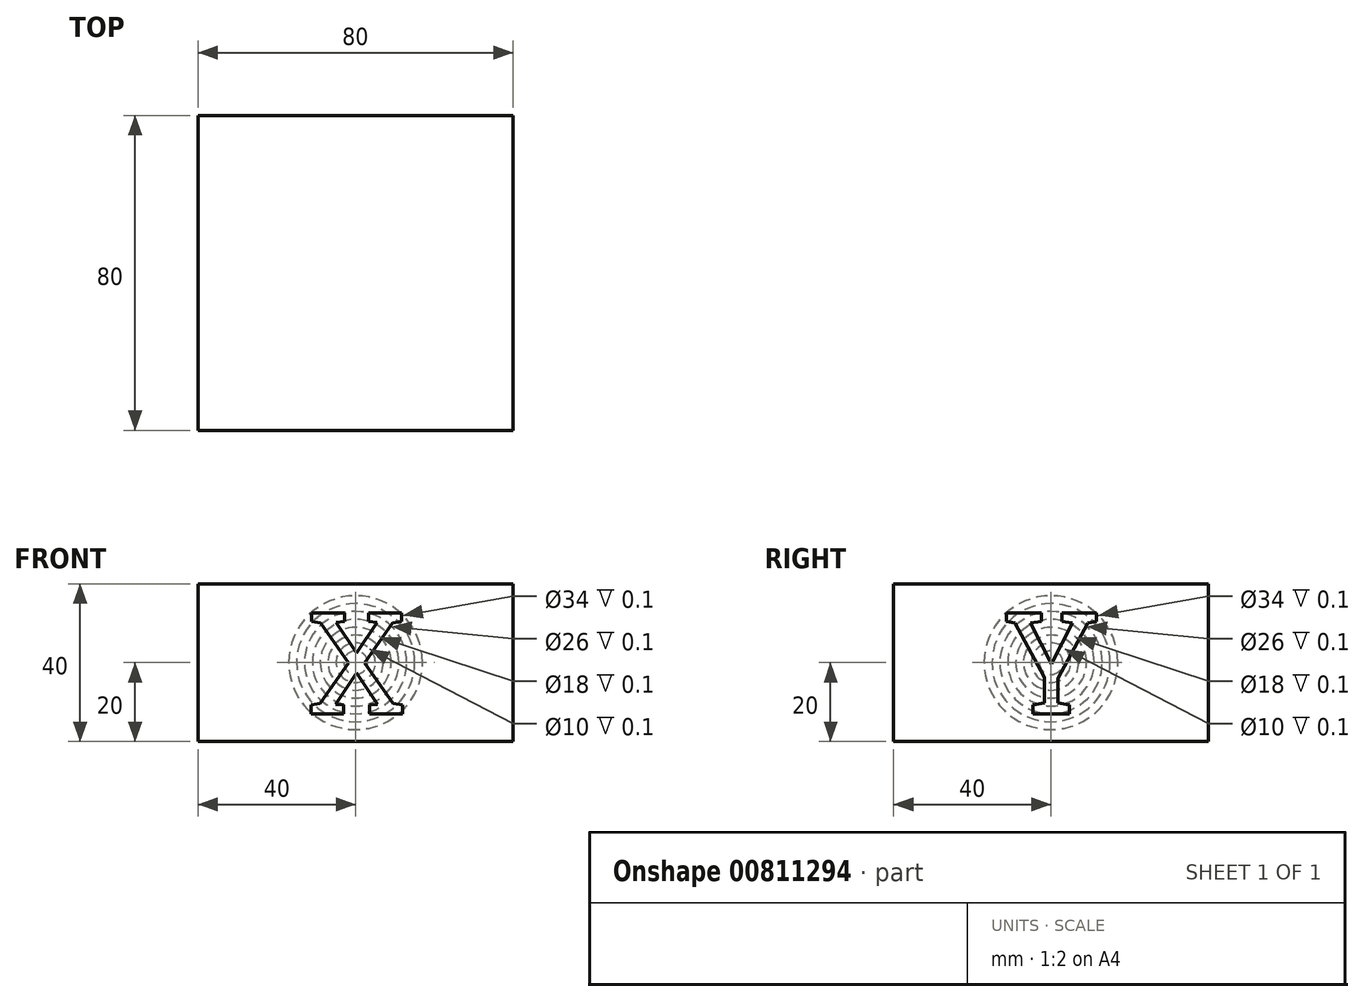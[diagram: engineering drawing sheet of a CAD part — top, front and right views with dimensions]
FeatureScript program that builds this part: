
annotation { "Feature Type Name" : "Feature", "Feature Type Description" : "" }
export const myFeature = defineFeature(function(context is Context, id is Id, definition is map)
    precondition{}
    {
        {
            var Q0;
            Q0=qCreatedBy(makeId("Top.planeOp"),FACE);
            var sketch = newSketch(context, id + "F0", { "sketchPlane" : qUnion([Q0])});
            skLineSegment(sketch, "E0.bottom", {"start": v(-40, 40) * mm, "end": v(40, 40) * mm});
            skLineSegment(sketch, "E0.top", {"start": v(-40, -40) * mm, "end": v(40, -40) * mm});
            skLineSegment(sketch, "E0.left", {"start": v(-40, 40) * mm, "end": v(-40, -40) * mm});
            skLineSegment(sketch, "E0.right", {"start": v(40, 40) * mm, "end": v(40, -40) * mm});
            skPoint(sketch, "E0.middle", {"position": v(0, 0) * mm});
            skSolve(sketch);
        }
        {
            var Q0;
            Q0=qSketchRegion(id+"F0",true);
            extrude(context, id + "F1", {"entities" : qUnion([Q0]), "depth" : 40 * mm, "offsetDistance" : 25 * mm});
        }
        {
            var Q0;
            Q0=makeQuery(id+"F1.opExtrude","SWEPT_FACE",FACE,{"disambiguationData":[OSD([sQuery(id+"F0.wireOp",EDGE,"E0.top")])]});
            var sketch = newSketch(context, id + "F2", { "sketchPlane" : qUnion([Q0])});
            skText(sketch, "E1", { "text": "X", "fontName": "RobotoSlab-Regular.ttf"});
            skLineSegment(sketch, "E2", {"start": v(0, 40) * mm, "end": v(0, 33) * mm});
            skLineSegment(sketch, "E3", {"start": v(0, 0) * mm, "end": v(0, 7) * mm, "construction": true});
            const initialGuessF2  = {"E1": [-0.01212, 0.007, 1, 0, 0.026]};
            skSetInitialGuess(sketch, initialGuessF2);
            skSolve(sketch);
        }
        {
            var Q0;
            Q0=makeQuery(id+"F2.imprint","IMPRINT",FACE,{"disambiguationData":[TD([[makeQuery(id+"F2.imprint","IMPRINT",EDGE,{"derivedFrom":sQuery(id+"F2.wireOp",EDGE,"E1.sketch_text.stroke-0")}),-1.0]])]});
            extrude(context, id + "F3", {"entities" : qUnion([Q0]), "operationType" : NewBodyOperationType.REMOVE, "oppositeDirection" : true, "depth" : 0.1 * mm, "offsetDistance" : 25 * mm});
        }
        {
            var Q0;
            Q0=makeQuery(id+"F1.opExtrude","SWEPT_FACE",FACE,{"disambiguationData":[OSD([sQuery(id+"F0.wireOp",EDGE,"E0.bottom")])]});
            var sketch = newSketch(context, id + "F4", { "sketchPlane" : qUnion([Q0])});
            skCircle(sketch, "E4", {"center": v(0, 20) * mm, "radius": 9 * mm});
            skCircle(sketch, "E5", {"center": v(0, 20) * mm, "radius": 7 * mm});
            skCircle(sketch, "E6", {"center": v(0, 20) * mm, "radius": 3 * mm});
            skCircle(sketch, "E7", {"center": v(0, 20) * mm, "radius": 5 * mm});
            skCircle(sketch, "E8", {"center": v(0, 20) * mm, "radius": 13 * mm});
            skCircle(sketch, "E9", {"center": v(0, 20) * mm, "radius": 11 * mm});
            skCircle(sketch, "E10", {"center": v(0, 20) * mm, "radius": 17 * mm});
            skCircle(sketch, "E11", {"center": v(0, 20) * mm, "radius": 15 * mm});
            skSolve(sketch);
        }
        {
            var Q0;
            Q0=makeQuery(id+"F4.imprint","IMPRINT",FACE,{"disambiguationData":[TD([[makeQuery(id+"F4.imprint","IMPRINT",EDGE,{"derivedFrom":sQuery(id+"F4.wireOp",EDGE,"E6")}),-1.0]])]});
            var Q1;
            Q1=makeQuery(id+"F4.imprint","IMPRINT",FACE,{"disambiguationData":[TD([[makeQuery(id+"F4.imprint","IMPRINT",EDGE,{"derivedFrom":sQuery(id+"F4.wireOp",EDGE,"E4")}),1.0]])]});
            var Q2;
            Q2=makeQuery(id+"F4.imprint","IMPRINT",FACE,{"disambiguationData":[TD([[makeQuery(id+"F4.imprint","IMPRINT",EDGE,{"derivedFrom":sQuery(id+"F4.wireOp",EDGE,"E8")}),1.0]])]});
            var Q3;
            Q3=makeQuery(id+"F4.imprint","IMPRINT",FACE,{"disambiguationData":[TD([[makeQuery(id+"F4.imprint","IMPRINT",EDGE,{"derivedFrom":sQuery(id+"F4.wireOp",EDGE,"E10")}),1.0]])]});
            extrude(context, id + "F5", {"entities" : qUnion([Q0, Q1, Q2, Q3]), "operationType" : NewBodyOperationType.REMOVE, "oppositeDirection" : true, "depth" : 0.1 * mm, "offsetDistance" : 25 * mm});
        }
        {
            var Q0;
            Q0=makeQuery(id+"F1.opExtrude","SWEPT_FACE",FACE,{"disambiguationData":[OSD([sQuery(id+"F0.wireOp",EDGE,"E0.right")])]});
            var sketch = newSketch(context, id + "F6", { "sketchPlane" : qUnion([Q0])});
            skText(sketch, "E12", { "text": "Y", "fontName": "RobotoSlab-Regular.ttf"});
            const initialGuessF6  = {"E12": [-0.0123, 0.007, 1, 0, 0.026]};
            skSetInitialGuess(sketch, initialGuessF6);
            skSolve(sketch);
        }
        {
            var Q0;
            Q0=makeQuery(id+"F6.imprint","IMPRINT",FACE,{"disambiguationData":[TD([[makeQuery(id+"F6.imprint","IMPRINT",EDGE,{"derivedFrom":sQuery(id+"F6.wireOp",EDGE,"E12.sketch_text.stroke-0")}),-1.0]])]});
            extrude(context, id + "F7", {"entities" : qUnion([Q0]), "operationType" : NewBodyOperationType.REMOVE, "oppositeDirection" : true, "depth" : 0.1 * mm, "offsetDistance" : 25 * mm});
        }
        {
            var Q0;
            Q0=makeQuery(id+"F1.opExtrude","SWEPT_FACE",FACE,{"disambiguationData":[OSD([sQuery(id+"F0.wireOp",EDGE,"E0.left")])]});
            var sketch = newSketch(context, id + "F8", { "sketchPlane" : qUnion([Q0])});
            skCircle(sketch, "E13", {"center": v(0, 20) * mm, "radius": 9 * mm});
            skCircle(sketch, "E14", {"center": v(0, 20) * mm, "radius": 7 * mm});
            skCircle(sketch, "E15", {"center": v(0, 20) * mm, "radius": 3 * mm});
            skCircle(sketch, "E16", {"center": v(0, 20) * mm, "radius": 5 * mm});
            skCircle(sketch, "E17", {"center": v(0, 20) * mm, "radius": 13 * mm});
            skCircle(sketch, "E18", {"center": v(0, 20) * mm, "radius": 11 * mm});
            skCircle(sketch, "E19", {"center": v(0, 20) * mm, "radius": 17 * mm});
            skCircle(sketch, "E20", {"center": v(0, 20) * mm, "radius": 15 * mm});
            skSolve(sketch);
        }
        {
            var Q0;
            Q0=makeQuery(id+"F8.imprint","IMPRINT",FACE,{"disambiguationData":[TD([[makeQuery(id+"F8.imprint","IMPRINT",EDGE,{"derivedFrom":sQuery(id+"F8.wireOp",EDGE,"E15")}),-1.0]])]});
            var Q1;
            Q1=makeQuery(id+"F8.imprint","IMPRINT",FACE,{"disambiguationData":[TD([[makeQuery(id+"F8.imprint","IMPRINT",EDGE,{"derivedFrom":sQuery(id+"F8.wireOp",EDGE,"E13")}),1.0]])]});
            var Q2;
            Q2=makeQuery(id+"F8.imprint","IMPRINT",FACE,{"disambiguationData":[TD([[makeQuery(id+"F8.imprint","IMPRINT",EDGE,{"derivedFrom":sQuery(id+"F8.wireOp",EDGE,"E17")}),1.0]])]});
            var Q3;
            Q3=makeQuery(id+"F8.imprint","IMPRINT",FACE,{"disambiguationData":[TD([[makeQuery(id+"F8.imprint","IMPRINT",EDGE,{"derivedFrom":sQuery(id+"F8.wireOp",EDGE,"E19")}),1.0]])]});
            extrude(context, id + "F9", {"entities" : qUnion([Q0, Q1, Q2, Q3]), "operationType" : NewBodyOperationType.REMOVE, "oppositeDirection" : true, "depth" : 0.1 * mm, "offsetDistance" : 25 * mm});
        }
    });
